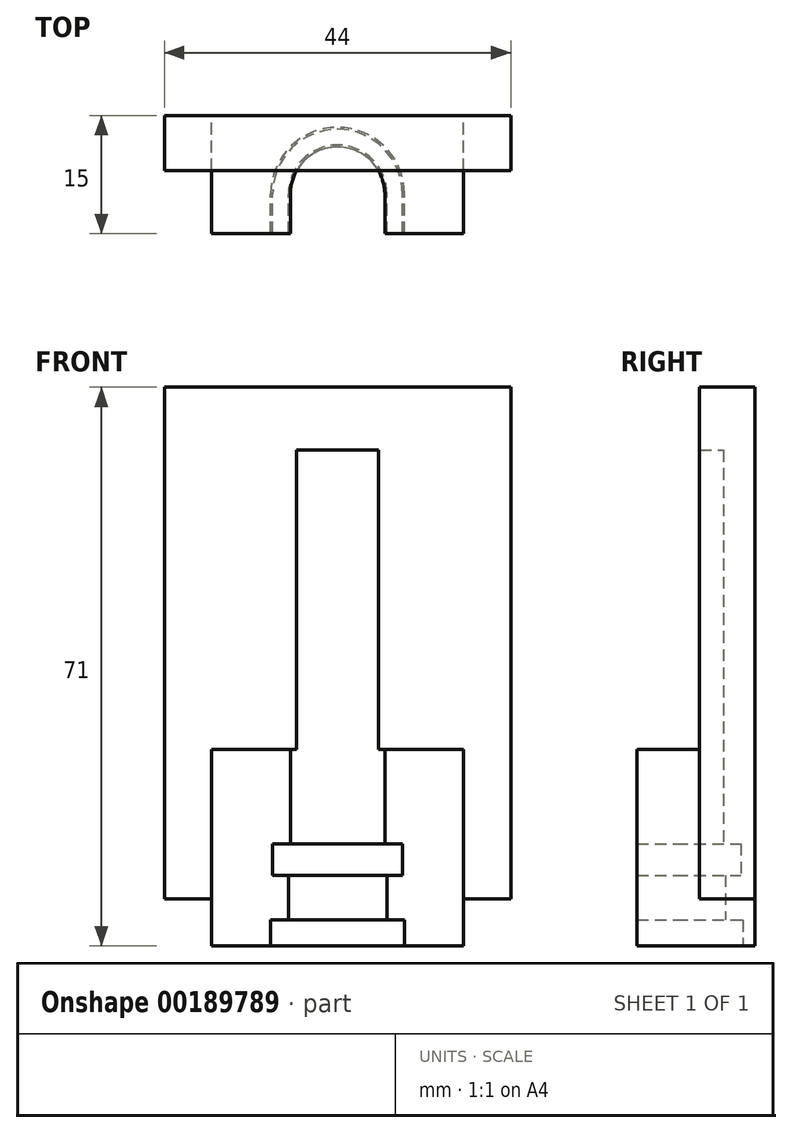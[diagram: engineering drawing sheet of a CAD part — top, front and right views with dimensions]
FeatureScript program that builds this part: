
annotation { "Feature Type Name" : "Feature", "Feature Type Description" : "" }
export const myFeature = defineFeature(function(context is Context, id is Id, definition is map)
    precondition{}
    {
        {
            var Q0;
            Q0=qCreatedBy(makeId("Front.planeOp"),FACE);
            var sketch = newSketch(context, id + "F0", { "sketchPlane" : qUnion([Q0])});
            skLineSegment(sketch, "E0", {"start": v(0, 0) * mm, "end": v(-16, 0) * mm});
            skLineSegment(sketch, "E1", {"start": v(-16, 0) * mm, "end": v(-16, 6) * mm});
            skLineSegment(sketch, "E2", {"start": v(-16, 6) * mm, "end": v(-22, 6) * mm});
            skLineSegment(sketch, "E3", {"start": v(-22, 6) * mm, "end": v(-22, 71) * mm});
            skLineSegment(sketch, "E4", {"start": v(-22, 71) * mm, "end": v(0, 71) * mm});
            skLineSegment(sketch, "E5.MirrorCS", {"start": v(22, 71) * mm, "end": v(0, 71) * mm});
            skLineSegment(sketch, "E6.MirrorCS", {"start": v(22, 6) * mm, "end": v(22, 71) * mm});
            skLineSegment(sketch, "E7.MirrorCS", {"start": v(16, 6) * mm, "end": v(22, 6) * mm});
            skLineSegment(sketch, "E8.MirrorCS", {"start": v(16, 0) * mm, "end": v(16, 6) * mm});
            skLineSegment(sketch, "E9.MirrorCS", {"start": v(0, 0) * mm, "end": v(16, 0) * mm});
            skSolve(sketch);
        }
        {
            var Q0;
            Q0 = qSketchRegion(id + "F0", true);
            extrude(context, id + "F1", {"entities" : qUnion([Q0]), "depth" : 7 * mm});
        }
        {
            var Q0;
            Q0=makeQuery(id+"F1.opExtrude","SWEPT_FACE",FACE,{"disambiguationData":[OSD([sQuery(id+"F0.wireOp",EDGE,"E0"),sQuery(id+"F0.wireOp",EDGE,"E9.MirrorCS")])]});
            var sketch = newSketch(context, id + "F2", { "sketchPlane" : qUnion([Q0])});
            skLineSegment(sketch, "E10.bottom", {"start": v(-16, 7) * mm, "end": v(16, 7) * mm});
            skLineSegment(sketch, "E10.top", {"start": v(-16, 10) * mm, "end": v(16, 10) * mm});
            skLineSegment(sketch, "E10.left", {"start": v(-16, 7) * mm, "end": v(-16, 10) * mm});
            skLineSegment(sketch, "E10.right", {"start": v(16, 7) * mm, "end": v(16, 10) * mm});
            skSolve(sketch);
        }
        {
            var Q0;
            Q0 = qSketchRegion(id + "F2", true);
            extrude(context, id + "F3", {"entities" : qUnion([Q0]), "operationType" : NewBodyOperationType.ADD, "oppositeDirection" : true, "depth" : 25 * mm});
        }
        {
            var Q0;
            Q0=makeQuery(id+"F3.boolean.opBoolean","MERGE",FACE,{"derivedFrom":[makeQuery(id+"F1.opExtrude","SWEPT_FACE",FACE,{"disambiguationData":[OSD([sQuery(id+"F0.wireOp",EDGE,"E0"),sQuery(id+"F0.wireOp",EDGE,"E9.MirrorCS")])]}),makeQuery(id+"F3.opExtrude","CAP_FACE",FACE,{"disambiguationData":[OSD([sQuery(id+"F2.wireOp",EDGE,"E10.bottom"),sQuery(id+"F2.wireOp",EDGE,"E10.top"),sQuery(id+"F2.wireOp",EDGE,"E10.left"),sQuery(id+"F2.wireOp",EDGE,"E10.right")])],"isStart":true})]});
            var sketch = newSketch(context, id + "F4", { "sketchPlane" : qUnion([Q0])});
            skCircle(sketch, "E11", {"center": v(0, 10) * mm, "radius": 8.5 * mm});
            skSolve(sketch);
        }
        {
            var Q0;
            Q0 = qSketchRegion(id + "F4", true);
            extrude(context, id + "F5", {"entities" : qUnion([Q0]), "operationType" : NewBodyOperationType.REMOVE, "oppositeDirection" : true, "depth" : 3.3 * mm});
        }
        {
            var Q0;
            Q0=makeQuery(id+"F5.boolean.opBoolean","COPY",FACE,{"derivedFrom":makeQuery(id+"F5.opExtrude","CAP_FACE",FACE,{"disambiguationData":[OSD([sQuery(id+"F4.wireOp",EDGE,"E11")])],"isStart":false})});
            var sketch = newSketch(context, id + "F6", { "sketchPlane" : qUnion([Q0])});
            skCircle(sketch, "E12", {"center": v(0, 10) * mm, "radius": 6.25 * mm});
            skSolve(sketch);
        }
        {
            var Q0;
            Q0 = qSketchRegion(id + "F6", true);
            extrude(context, id + "F7", {"entities" : qUnion([Q0]), "operationType" : NewBodyOperationType.REMOVE, "oppositeDirection" : true, "depth" : 5.7 * mm});
        }
        {
            var Q0;
            Q0=makeQuery(id+"F7.boolean.opBoolean","COPY",FACE,{"derivedFrom":makeQuery(id+"F7.opExtrude","CAP_FACE",FACE,{"disambiguationData":[OSD([sQuery(id+"F6.wireOp",EDGE,"E12")])],"isStart":false})});
            var sketch = newSketch(context, id + "F8", { "sketchPlane" : qUnion([Q0])});
            skCircle(sketch, "E13", {"center": v(0, 10) * mm, "radius": 8.25 * mm});
            skSolve(sketch);
        }
        {
            var Q0;
            Q0 = qSketchRegion(id + "F8", true);
            extrude(context, id + "F9", {"entities" : qUnion([Q0]), "operationType" : NewBodyOperationType.REMOVE, "oppositeDirection" : true, "depth" : 4 * mm});
        }
        {
            var Q0;
            Q0=makeQuery(id+"F9.boolean.opBoolean","COPY",FACE,{"derivedFrom":makeQuery(id+"F9.opExtrude","CAP_FACE",FACE,{"disambiguationData":[OSD([sQuery(id+"F8.wireOp",EDGE,"E13")])],"isStart":false})});
            var sketch = newSketch(context, id + "F10", { "sketchPlane" : qUnion([Q0])});
            skCircle(sketch, "E14", {"center": v(0, 10) * mm, "radius": 6 * mm});
            skSolve(sketch);
        }
        {
            var Q0;
            Q0 = qSketchRegion(id + "F10", true);
            extrude(context, id + "F11", {"entities" : qUnion([Q0]), "operationType" : NewBodyOperationType.REMOVE, "oppositeDirection" : true, "depth" : 50 * mm});
        }
        {
            var Q0;
            {var subQ3=sQuery(id+"F2.wireOp",EDGE,"E10.top");Q0=makeQuery(id+"F11.boolean.opBoolean","SPLIT",FACE,{"disambiguationData":[TD([makeQuery(id+"F1.opExtrude","SWEPT_FACE",FACE,{"disambiguationData":[OSD([sQuery(id+"F0.wireOp",EDGE,"E1")])]})])],"derivedFrom":makeQuery(id+"F3.opExtrude","SWEPT_FACE",FACE,{"disambiguationData":[OSD([subQ3])]})});}
            var Q1;
            {var subQ3=sQuery(id+"F2.wireOp",EDGE,"E10.top");Q1=makeQuery(id+"F11.boolean.opBoolean","SPLIT",FACE,{"disambiguationData":[TD([makeQuery(id+"F1.opExtrude","SWEPT_FACE",FACE,{"disambiguationData":[OSD([sQuery(id+"F0.wireOp",EDGE,"E8.MirrorCS")])]})])],"derivedFrom":makeQuery(id+"F3.opExtrude","SWEPT_FACE",FACE,{"disambiguationData":[OSD([subQ3])]})});}
            extrude(context, id + "F12", {"entities" : qUnion([Q0, Q1]), "operationType" : NewBodyOperationType.ADD, "depth" : 5 * mm});
        }
    });
